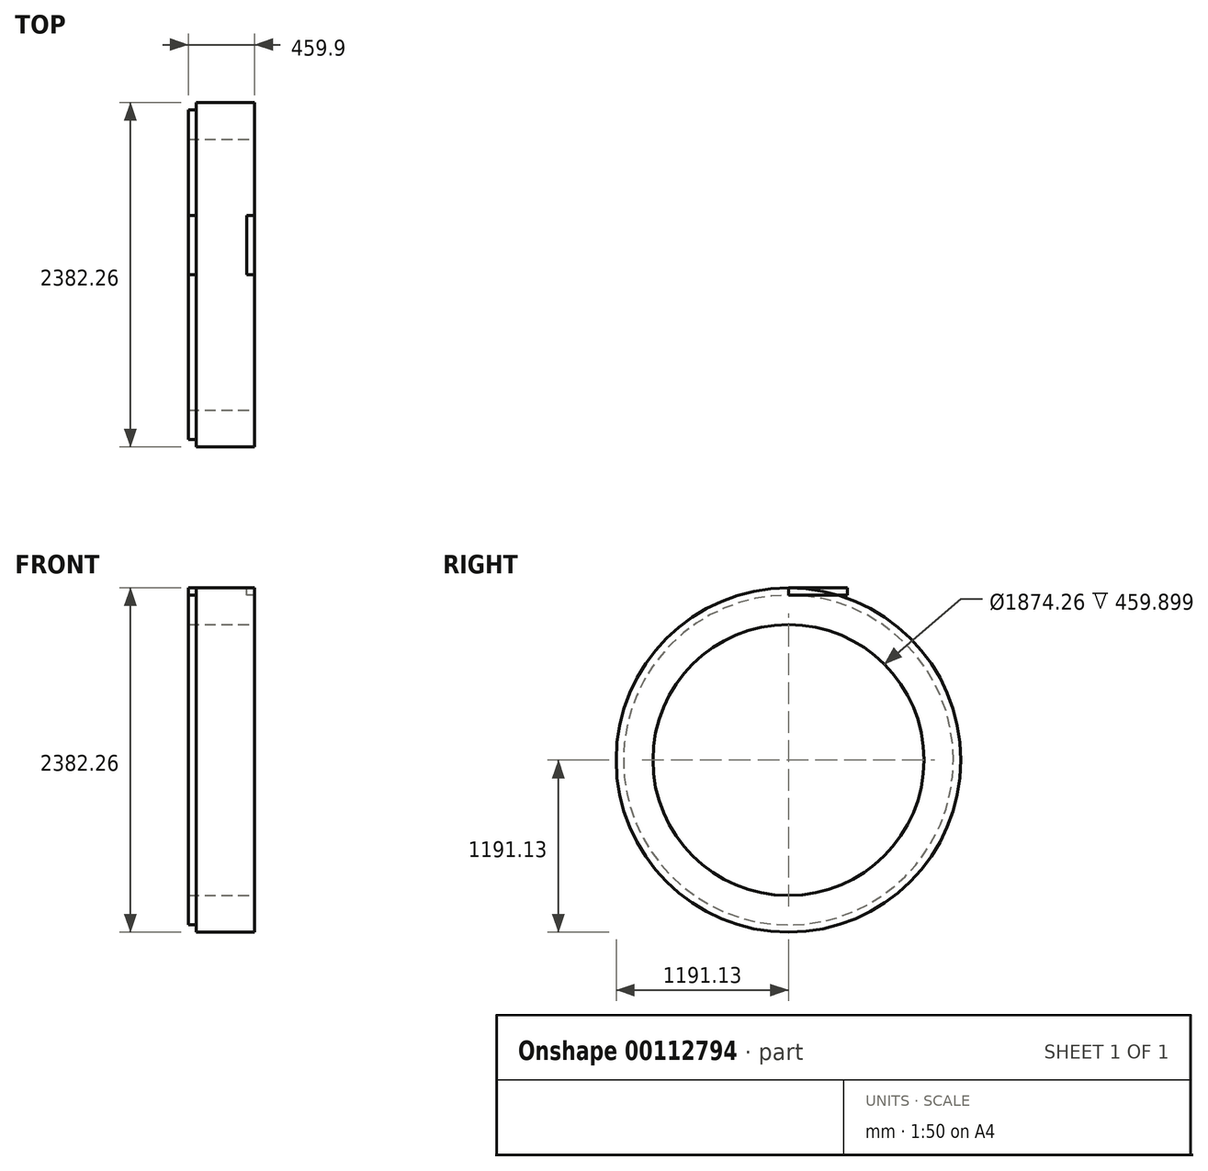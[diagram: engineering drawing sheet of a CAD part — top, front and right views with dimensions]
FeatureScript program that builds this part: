
annotation { "Feature Type Name" : "Feature", "Feature Type Description" : "" }
export const myFeature = defineFeature(function(context is Context, id is Id, definition is map)
    precondition{}
    {
        {
            var Q0;
            Q0=qCreatedBy(makeId("Front.planeOp"),FACE);
            var sketch = newSketch(context, id + "F0", { "sketchPlane" : qUnion([Q0])});
            skArc(sketch, "E0", {"start": v(93.88, 0) * mm, "mid": v(-1.14, 57.38) * mm, "end": v(-96.15, 0) * mm});
            skLineSegment(sketch, "E1", {"start": v(-96.15, 0) * mm, "end": v(-177.11, -21.7) * mm});
            skLineSegment(sketch, "E2", {"start": v(-177.11, -21.7) * mm, "end": v(-231.09, -21.7) * mm});
            skLineSegment(sketch, "E3", {"start": v(-231.09, -21.7) * mm, "end": v(-312.05, 0) * mm});
            skLineSegment(sketch, "E4", {"start": v(93.88, 0) * mm, "end": v(174.84, -21.7) * mm});
            skLineSegment(sketch, "E5", {"start": v(174.84, -21.7) * mm, "end": v(228.81, -21.7) * mm});
            skLineSegment(sketch, "E6", {"start": v(228.81, -21.7) * mm, "end": v(309.78, 0) * mm});
            skSolve(sketch);
        }
        {
            var Q0;
            Q0=qCreatedBy(makeId("Right.planeOp"),FACE);
            var sketch = newSketch(context, id + "F1", { "sketchPlane" : qUnion([Q0])});
            skFitSpline(sketch, "E7", {"points": [v(0, 0) * mm, v(100.53, 0) * mm, v(166.73, -22.96) * mm, v(342.7, -19.27) * mm, v(408.72, 0) * mm], "startDerivative": vector(441.95, 37.24) * mm, "endDerivative": vector(256.93, 100.3) * mm});
            skLineSegment(sketch, "E8", {"start": v(408.72, 0) * mm, "end": v(408.72, -57.17) * mm});
            skLineSegment(sketch, "E9", {"start": v(408.72, -57.17) * mm, "end": v(0, -57.17) * mm});
            skLineSegment(sketch, "E10", {"start": v(0, -57.17) * mm, "end": v(0, 0) * mm});
            skSolve(sketch);
        }
        {
            var Q0;
            Q0 = qSketchRegion(id + "F0", true);
            var Q1;
            Q1 = qConstructionFilter(qBodyType(qCreatedBy(id + "F0" ,EDGE), BodyType.WIRE), ConstructionObject.NO);
            var Q2;
            Q2 = qConstructionFilter(qBodyType(qCreatedBy(id + "F1" ,EDGE), BodyType.WIRE), ConstructionObject.NO);
            sweep(context, id + "F2", {"bodyType" : ToolBodyType.SURFACE, "profiles" : qUnion([Q0]), "surfaceProfiles" : qUnion([Q1]), "path" : qUnion([Q2]), "keepProfileOrientation" : true});
        }
        {
            var Q0;
            Q0=makeQuery(id+"F2.opSweep","SWEPT_FACE",FACE,{"disambiguationData":[OSD([sQuery(id+"F0.wireOp",EDGE,"E2"),sQuery(id+"F1.wireOp",EDGE,"E9")])]});
            var sketch = newSketch(context, id + "F3", { "sketchPlane" : qUnion([Q0])});
            skLineSegment(sketch, "E11.left", {"start": v(-231.09, 0) * mm, "end": v(-231.09, 408.72) * mm});
            skLineSegment(sketch, "E11.right", {"start": v(228.81, 0) * mm, "end": v(228.81, 408.72) * mm});
            skLineSegment(sketch, "E12", {"start": v(-231.09, 0) * mm, "end": v(-177.11, 0) * mm});
            skLineSegment(sketch, "E13", {"start": v(-177.11, 0) * mm, "end": v(-177.11, 408.72) * mm});
            skLineSegment(sketch, "E14", {"start": v(-177.11, 408.72) * mm, "end": v(-231.09, 408.72) * mm});
            skLineSegment(sketch, "E15", {"start": v(228.81, 0) * mm, "end": v(174.84, 0) * mm});
            skLineSegment(sketch, "E16", {"start": v(174.84, 0) * mm, "end": v(174.84, 408.72) * mm});
            skLineSegment(sketch, "E17", {"start": v(174.84, 408.72) * mm, "end": v(228.81, 408.72) * mm});
            skSolve(sketch);
        }
        {
            var Q0;
            Q0 = qSketchRegion(id + "F3", true);
            extrude(context, id + "F4", {"entities" : qUnion([Q0]), "oppositeDirection" : true, "depth" : 50.8 * mm});
        }
        {
            var Q0;
            Q0=qCreatedBy(makeId("Top.planeOp"),FACE);
            cPlane(context, id + "F5", {"entities" : qUnion([Q0]), "cplaneType" : CPlaneType.OFFSET, "offset" : 1270 * mm, "oppositeDirection" : true, "width" : 152.4 * mm, "height" : 152.4 * mm});
        }
        {
            var Q0;
            Q0=qCreatedBy(id+"F5.planeOp",FACE);
            var sketch = newSketch(context, id + "F6", { "sketchPlane" : qUnion([Q0])});
            skPoint(sketch, "E18", {"position": v(0, 0) * mm});
            skLineSegment(sketch, "E19", {"start": v(34.18, 0) * mm, "end": v(-29.21, 0) * mm});
            skSolve(sketch);
        }
        {
            var Q0;
            Q0=makeQuery(id+"F4.opExtrude","SWEPT_FACE",FACE,{"disambiguationData":[OSD([sQuery(id+"F3.wireOp",EDGE,"E12")])]});
            var sketch = newSketch(context, id + "F7", { "sketchPlane" : qUnion([Q0])});
            skLineSegment(sketch, "E20.bottom", {"start": v(-231.09, -78.87) * mm, "end": v(228.81, -78.87) * mm});
            skLineSegment(sketch, "E20.top", {"start": v(-231.09, -332.87) * mm, "end": v(228.81, -332.87) * mm});
            skLineSegment(sketch, "E20.left", {"start": v(-231.09, -78.87) * mm, "end": v(-231.09, -332.87) * mm});
            skLineSegment(sketch, "E20.right", {"start": v(228.81, -78.87) * mm, "end": v(228.81, -332.87) * mm});
            skSolve(sketch);
        }
        {
            var Q0;
            {var subQ4=sQuery(id+"F7.wireOp",EDGE,"E20.top");Q0=makeQuery(id+"F7.imprint","IMPRINT",FACE,{"disambiguationData":[TD([[makeQuery(id+"F7.imprint","IMPRINT",EDGE,{"derivedFrom":subQ4}),1.0]])]});}
            var Q1;
            Q1=sQuery(id+"F6.wireOp",EDGE,"E19");
            revolve(context, id + "F8", {"entities" : qUnion([Q0]), "axis" : qUnion([Q1]), "revolveType" : RevolveType.FULL});
        }
    });
